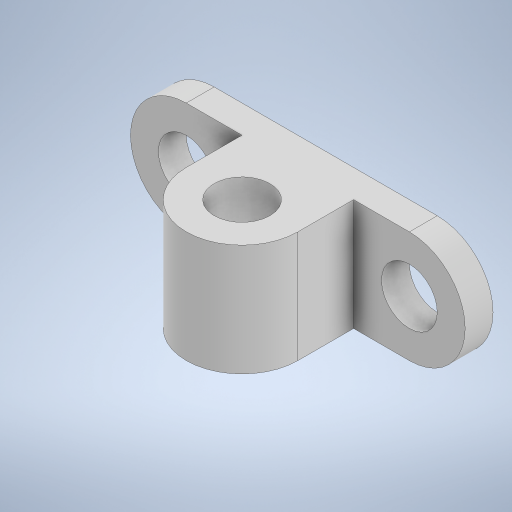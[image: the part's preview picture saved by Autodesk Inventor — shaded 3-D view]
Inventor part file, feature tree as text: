
AUTODESK INVENTOR PART (.ipt)
format: ipt  version: 2024 (Build 280153000, 153)  size: 259,072 bytes
history: native  units: mm
features: extrude x5, sketch x5
ambient origin geometry x8: Origin, YZ Plane, XZ Plane, XY Plane, X Axis, Y Axis, Z Axis, Center Point
bodies: Solid1 (feature_tree)
feature tree (10):
  extrude  "Extrusion1"  Depth=40.0mm
  extrude  "Extrusion2"  Depth=20.0mm
  extrude  "Extrusion3"  Depth=10.0mm TaperAngle=0.0deg
  extrude  "Extrusion4"  Depth=40.0mm
  extrude  "Extrusion5"  Depth=20.0mm TaperAngle=0.0deg
  sketch  "Sketch1"  dims[d1=80.0mm d2=40.0mm]
  sketch  "Sketch2"  dims[d3=10.0mm d4=0.0mm d6=20.0mm]
  sketch  "Sketch3"  dims[d7=20.0mm d8=10.0mm d9=0.0mm]
  sketch  "Sketch4"  dims[d10=40.0mm d11=40.0mm]
  sketch  "Sketch5"  dims[d12=20.0mm d13=20.0mm d14=0.0mm d15=40.0mm d16=0.0mm d17=20.0mm d18=40.0mm d19=0.0mm]
